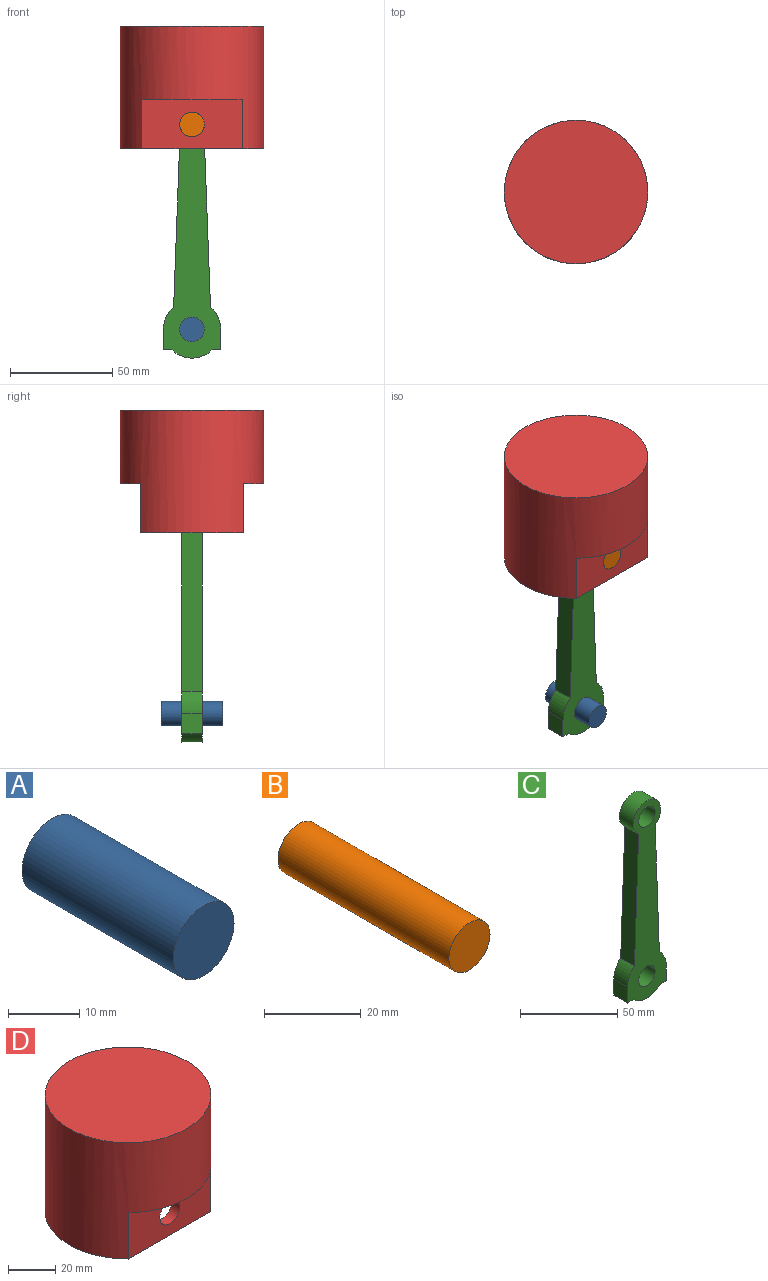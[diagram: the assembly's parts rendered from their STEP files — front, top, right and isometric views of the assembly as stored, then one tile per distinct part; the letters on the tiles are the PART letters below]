
ASSEMBLY  parts=4 mates=3
PART A: 3 faces, bbox 12x30x12 mm
  f0: cylinder r=6mm len=30mm, axis (0,1,0), area 1131mm2, adj f1,f2
  f1: plane 12x12mm, normal (0,-1,0), area 113.1mm2, adj f0
  f2: plane 12x12mm, normal (0,1,0), area 113.1mm2, adj f0
PART B: 3 faces, bbox 12x50x12 mm
  f0: cylinder r=6mm len=50mm, axis (0,1,0), area 1885mm2, adj f1,f2
  f1: plane 12x12mm, normal (0,-1,0), area 113.1mm2, adj f0
  f2: plane 12x12mm, normal (0,1,0), area 113.1mm2, adj f0
PART C: 14 faces, bbox 28x10x124 mm
  f0: plane 81.28x10mm, normal (1,0,0.04), area 813.3mm2, adj f1,f10,f12,f13
  f1: cylinder r=10mm len=20mm, axis (0,1,0), area 499.6mm2, adj f0,f2,f12,f13
  f2: plane 81.28x10mm, normal (-1,0,0.04), area 813.3mm2, adj f1,f3,f12,f13
  f3: cylinder r=14mm len=10.72mm, axis (0,1,0), area 122.2mm2, adj f2,f4,f12,f13
  f4: plane 10x10mm, normal (-1,0,0), area 100mm2, adj f3,f5,f12,f13
  f5: plane 10x4.2mm, normal (0,0,-1), area 42mm2, adj f4,f6,f12,f13
  f6: cylinder r=14mm len=19.6mm, axis (0,1,0), area 217.1mm2, adj f5,f7,f12,f13
  f7: plane 10x4.2mm, normal (0,0,-1), area 42mm2, adj f6,f8,f12,f13
  f8: plane 10x10mm, normal (1,0,0), area 100mm2, adj f7,f10,f12,f13
  f9: cylinder r=6mm len=12mm, axis (0,1,0), area 377mm2, adj f12,f13
  f10: cylinder r=14mm len=10.72mm, axis (0,1,0), area 122.2mm2, adj f0,f8,f12,f13
  f11: cylinder r=6mm len=12mm, axis (0,1,0), area 377mm2, adj f12,f13
  f12: plane 124x28mm, normal (0,-1,0), area 1892.3mm2, adj f0,f1,f2,f3,f4,f5,f6,f7
  f13: plane 124x28mm, normal (0,1,0), area 1892.3mm2, adj f0,f1,f2,f3,f4,f5,f6,f7
PART D: 14 faces, bbox 70x70x60 mm
  f0: plane 70x50mm, normal (0,0,-1), area 966mm2, adj f1,f3,f6,f7,f8,f9,f10
  f1: cylinder r=35mm len=70mm, axis (0,0,-1), area 10590mm2, adj f0,f2,f3,f4,f5,f6
  f2: plane 70x70mm, normal (0,0,1), area 3848.5mm2, adj f1
  f3: plane 48.99x24mm, normal (0,-1,0), area 1062.7mm2, adj f0,f1,f4,f13
  f4: plane 48.99x10mm, normal (0,0,-1), area 337.2mm2, adj f1,f3
  f5: plane 48.99x10mm, normal (0,0,-1), area 337.2mm2, adj f1,f6
  f6: plane 48.99x24mm, normal (0,1,0), area 1062.7mm2, adj f0,f1,f5,f12
  f7: plane 44.72x24mm, normal (0,1,0), area 960.2mm2, adj f0,f8,f10,f11,f13
  f8: cylinder r=30mm len=40mm, axis (0,0,-1), area 1050.8mm2, adj f0,f7,f9,f11
  f9: plane 44.72x24mm, normal (0,-1,0), area 960.2mm2, adj f0,f8,f10,f11,f12
  f10: cylinder r=30mm len=40mm, axis (0,0,-1), area 1050.8mm2, adj f0,f7,f9,f11
  f11: plane 60x40mm, normal (0,0,-1), area 2207.9mm2, adj f7,f8,f9,f10
  f12: cylinder r=6mm len=12mm, axis (0,-1,0), area 188.5mm2, adj f6,f9
  f13: cylinder r=6mm len=12mm, axis (0,-1,0), area 188.5mm2, adj f3,f7
PLACE A t=(167.54,93.88,22.94)mm
PLACE B t=(167.54,93.88,22.94)mm
PLACE C t=(167.54,93.88,22.94)mm
PLACE D t=(167.54,93.88,22.94)mm
MATE revolute D.f12 <-> B.f0  axis (0,-1,0) through (167.54,68.88,184.94)mm
MATE fastened B.f0 <-> C.f1  axis (0,1,0) through (167.54,93.88,184.94)mm
MATE revolute A.f0 <-> C.f3  axis (0,1,0) through (167.54,93.88,84.94)mm
